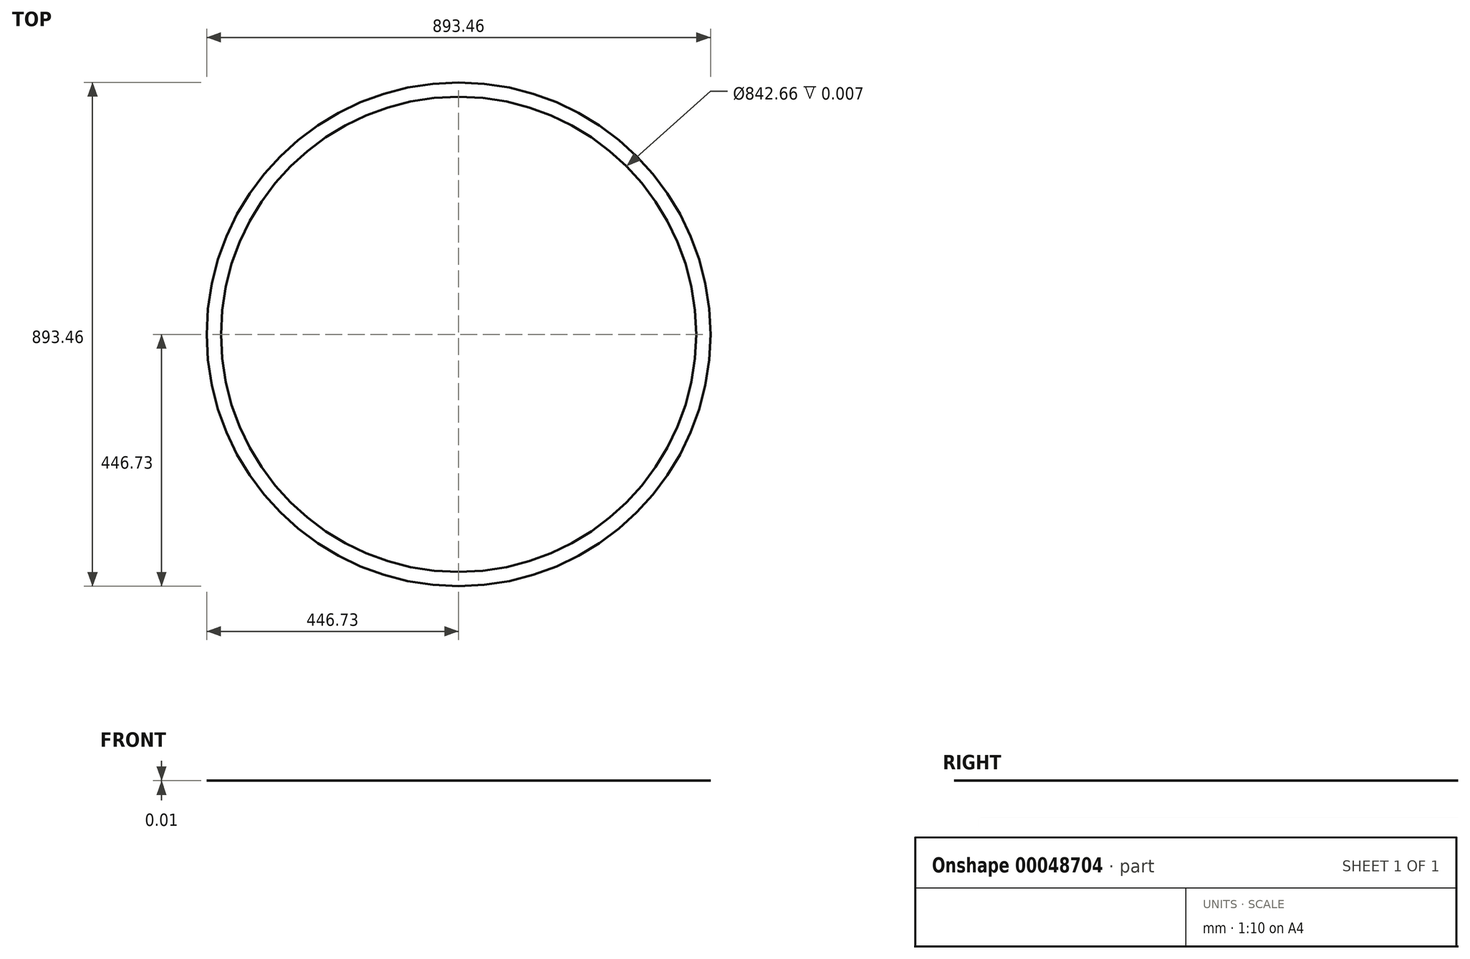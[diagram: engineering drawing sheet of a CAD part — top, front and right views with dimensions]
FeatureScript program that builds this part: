
annotation { "Feature Type Name" : "Feature", "Feature Type Description" : "" }
export const myFeature = defineFeature(function(context is Context, id is Id, definition is map)
    precondition{}
    {
        {
            var Q0;
            Q0=qCreatedBy(makeId("Top.planeOp"),FACE);
            var sketch = newSketch(context, id + "F0", { "sketchPlane" : qUnion([Q0])});
            skCircle(sketch, "E0", {"center": v(0, 0) * mm, "radius": 446.73 * mm});
            skCircle(sketch, "E1", {"center": v(0, 0) * mm, "radius": 421.33 * mm});
            skSolve(sketch);
        }
        {
            var Q0;
            Q0 = qSketchRegion(id + "F0", true);
            extrude(context, id + "F1", {"entities" : qUnion([Q0]), "depth" : 3 / 457.2 * mm});
        }
    });
